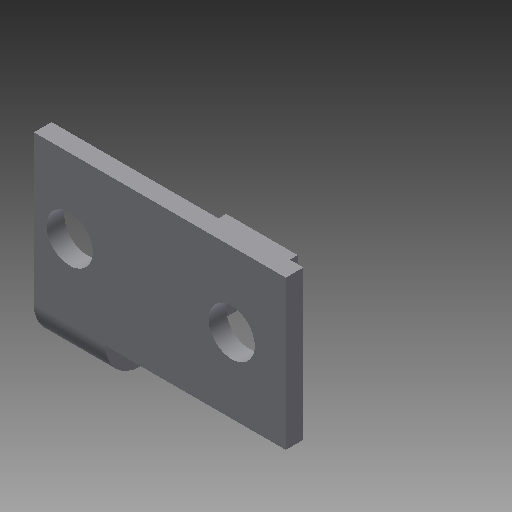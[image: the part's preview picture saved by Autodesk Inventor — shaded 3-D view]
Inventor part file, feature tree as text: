
AUTODESK INVENTOR PART (.ipt)
format: ipt  version: 2017 (Build 210142000, 142)  size: 151,552 bytes
history: native  units: in
note: dims shown in document units (in); Inventor stores cm internally (conversion verified against a paired STEP export)
features: sketch x5, sheet_metal_op x4, extrude x3, other x2
ambient origin geometry x8: Origin, YZ Plane, XZ Plane, XY Plane, X Axis, Y Axis, Z Axis, Center Point
bodies: Body1 (feature_tree)
feature tree (14):
  sheet_metal_op  "Face1"
  sheet_metal_op  "Flange1"
  extrude  "Extrusion3"  Depth=0.238in
  extrude  "Extrusion6"  Depth=0.305in
  extrude  "Extrusion8"  Depth=0.125in
  sketch  "Sketch1"  dims[d0=0.64in d1=0.238in]
  other  "Plate1"
  sketch  "Sketch2"  dims[d2=0.157in d3=0.305in]
  other  "Plate2"
  sheet_metal_op  "Bend1"
  sheet_metal_op  "Corner1"
  sketch  "Sketch4"  dims[d4=0.125in d5=0.125in]
  sketch  "Sketch7"  dims[d10=0.059in]
  sketch  "Sketch9"  dims[d11=0.059in d12=0.0295in d13=0.118in d14=0.059in d15=0.614in d16=90.0deg d17=0.059in d18=0.236in d19=0.059in d20=0.059in d21=0.248in d22=0.154in d23=0.059in d24=0.0in d32=0.6in d33=0.0in d39=0.154in d40=0.18in d41=0.248in d42=0.6in d43=0.0in]
